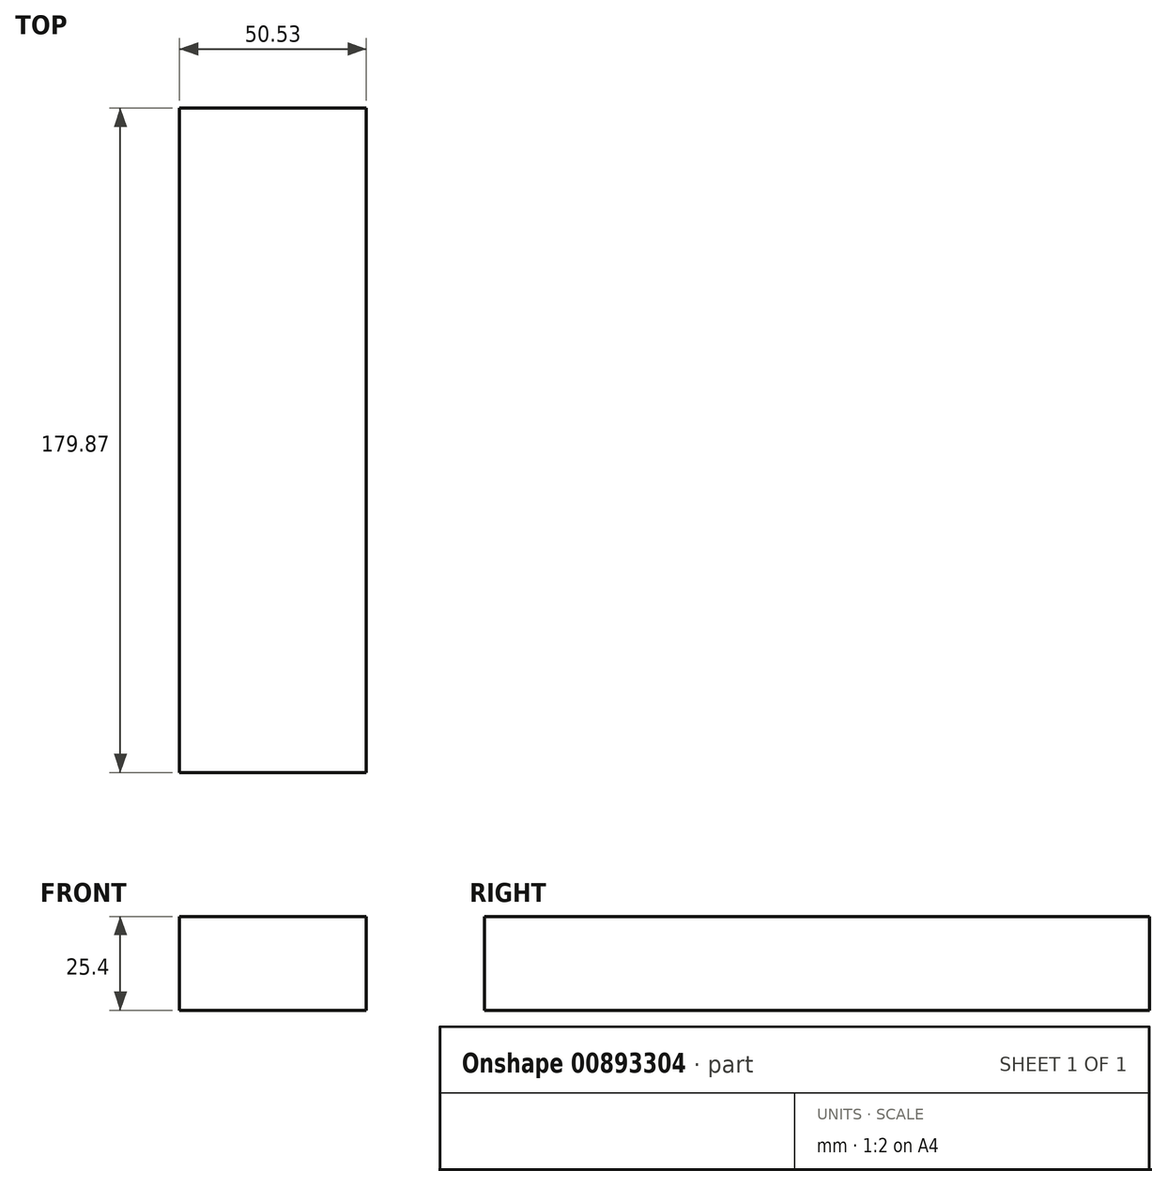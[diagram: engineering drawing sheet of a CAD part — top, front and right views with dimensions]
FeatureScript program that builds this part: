
annotation { "Feature Type Name" : "Feature", "Feature Type Description" : "" }
export const myFeature = defineFeature(function(context is Context, id is Id, definition is map)
    precondition{}
    {
        {
            var Q0;
            Q0=qCreatedBy(makeId("Top.planeOp"),FACE);
            var sketch = newSketch(context, id + "F0", { "sketchPlane" : qUnion([Q0])});
            skLineSegment(sketch, "E0.bottom", {"start": v(34.96, 91.96) * mm, "end": v(85.49, 91.96) * mm});
            skLineSegment(sketch, "E0.top", {"start": v(34.96, -87.9) * mm, "end": v(85.49, -87.9) * mm});
            skLineSegment(sketch, "E0.left", {"start": v(34.96, 91.96) * mm, "end": v(34.96, -87.9) * mm});
            skLineSegment(sketch, "E0.right", {"start": v(85.49, 91.96) * mm, "end": v(85.49, -87.9) * mm});
            skSolve(sketch);
        }
        {
            var Q0;
            Q0=makeQuery(id+"F0.imprint","IMPRINT",FACE,{"disambiguationData":[TD([[makeQuery(id+"F0.imprint","IMPRINT",EDGE,{"derivedFrom":sQuery(id+"F0.wireOp",EDGE,"E0.bottom")}),-1.0]])]});
            var sketch = newSketch(context, id + "F1", { "sketchPlane" : qUnion([Q0])});
            skSolve(sketch);
        }
        {
            var Q0;
            Q0=makeQuery(id+"F1.imprint","IMPRINT",FACE,{"disambiguationData":[TD([[makeQuery(id+"F1.imprint","IMPRINT",EDGE,{"derivedFrom":makeQuery(id+"F0.imprint","IMPRINT",EDGE,{"derivedFrom":sQuery(id+"F0.wireOp",EDGE,"E0.bottom")})}),-1.0]])]});
            extrude(context, id + "F2", {"entities" : qUnion([Q0]), "depth" : 25.4 * mm, "offsetDistance" : 25.4 * mm});
        }
    });
